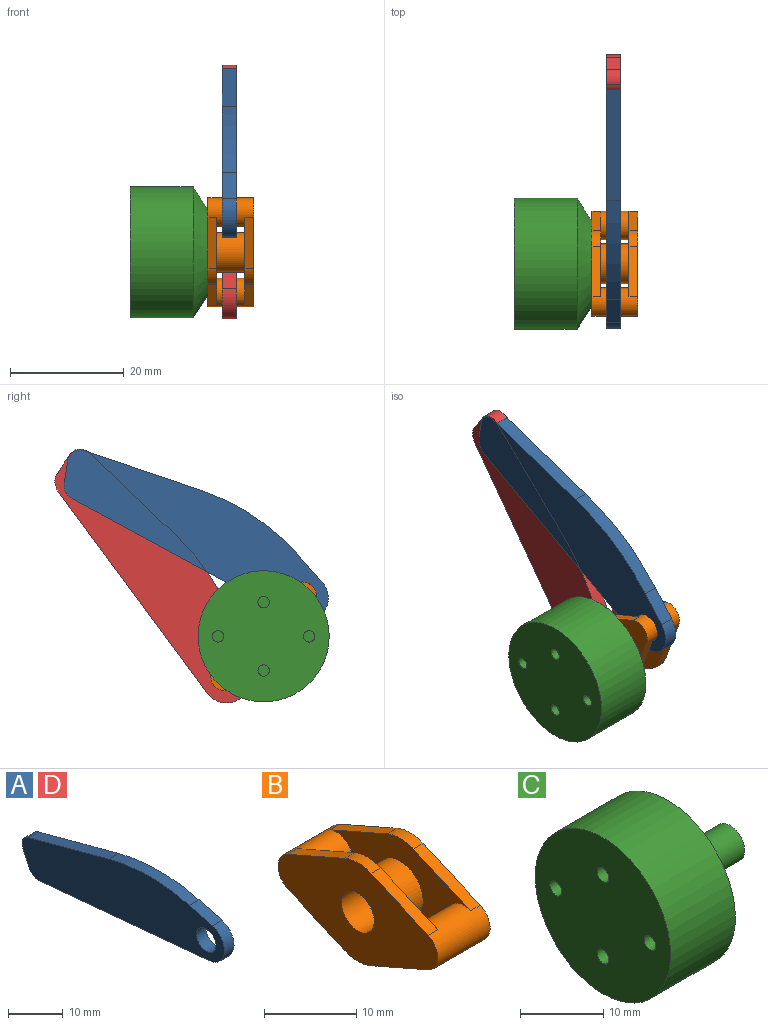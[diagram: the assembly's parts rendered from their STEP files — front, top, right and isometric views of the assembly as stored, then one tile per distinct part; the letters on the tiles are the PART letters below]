
ASSEMBLY  parts=4 mates=3
PART A: 11 faces, bbox 2.5x52.3x15.2 mm
  f0: plane 3.51x2.5mm, normal (0,0.91,-0.42), area 9.7mm2, adj f1,f7,f8,f9
  f1: cylinder r=2.28mm len=3.16mm, axis (-1,0,0), area 9.9mm2, adj f0,f2,f8,f9
  f2: plane 20.79x5.58mm, normal (0,0.26,0.97), area 53.8mm2, adj f1,f3,f8,f9
  f3: cylinder r=40.06mm len=20.78mm, axis (-1,0,0), area 52.5mm2, adj f2,f4,f8,f9
  f4: plane 5.97x2.5mm, normal (0,-0.26,0.97), area 15.5mm2, adj f3,f5,f8,f9
  f5: cylinder r=4.16mm len=8.15mm, axis (-1,0,0), area 29mm2, adj f4,f6,f8,f9
  f6: plane 43.96x4.06mm, normal (0,-0.09,-1), area 110.4mm2, adj f5,f7,f8,f9
  f7: cylinder r=2.72mm len=2.71mm, axis (-1,0,0), area 8.3mm2, adj f0,f6,f8,f9
  f8: plane 52.3x15.2mm, normal (1,0,0), area 524.7mm2, adj f0,f1,f2,f3,f4,f5,f6,f7
  f9: plane 52.3x15.2mm, normal (-1,0,0), area 524.7mm2, adj f0,f1,f2,f3,f4,f5,f6,f7
  f10: cylinder r=2.5mm len=5mm, axis (1,0,0), area 39.3mm2, adj f8,f9
PART B: 20 faces, bbox 8x24.5x13.1 mm
  f0: plane 8.76x3.83mm, normal (0,-0.4,0.92), area 14.3mm2, adj f7,f14,f15,f19
  f1: plane 8.76x3.83mm, normal (0,-0.4,-0.92), area 14.3mm2, adj f2,f7,f16,f18
  f2: cylinder r=5mm len=4.01mm, axis (-1,0,0), area 6.2mm2, adj f1,f10,f16,f18
  f3: plane 8.76x3.83mm, normal (0,0.4,-0.92), area 14.3mm2, adj f9,f11,f15,f19
  f4: plane 8.76x3.83mm, normal (0,0.4,0.92), area 14.3mm2, adj f5,f11,f16,f18
  f5: cylinder r=5mm len=4.01mm, axis (-1,0,0), area 6.2mm2, adj f4,f6,f16,f18
  f6: plane 8.76x3.83mm, normal (0,-0.4,0.92), area 14.3mm2, adj f5,f7,f16,f18
  f7: cylinder r=2.5mm len=8mm, axis (-1,0,0), area 95.9mm2, adj f0,f1,f6,f8,f15,f16,f18,f19
  f8: plane 8.76x3.83mm, normal (0,-0.4,-0.92), area 14.3mm2, adj f7,f9,f15,f19
  f9: cylinder r=5mm len=4.01mm, axis (-1,0,0), area 6.2mm2, adj f3,f8,f15,f19
  f10: plane 8.76x3.83mm, normal (0,0.4,-0.92), area 14.3mm2, adj f2,f11,f16,f18
  f11: cylinder r=2.5mm len=8mm, axis (-1,0,0), area 95.9mm2, adj f3,f4,f10,f12,f15,f16,f18,f19
  f12: plane 8.76x3.83mm, normal (0,0.4,0.92), area 14.3mm2, adj f11,f14,f15,f19
  f13: cylinder r=2.5mm len=8mm, axis (-1,0,0), area 125.7mm2, adj f15,f16
  f14: cylinder r=5mm len=4.01mm, axis (-1,0,0), area 6.2mm2, adj f0,f12,f15,f19
  f15: plane 24.53x13.09mm, normal (1,0,0), area 189mm2, adj f0,f3,f7,f8,f9,f11,f12,f13
  f16: plane 24.53x13.09mm, normal (-1,0,0), area 189mm2, adj f1,f2,f4,f5,f6,f7,f10,f11
  f17: cylinder r=3.5mm len=7mm, axis (1,0,0), area 110mm2, adj f18,f19
  f18: plane 21.53x13.09mm, normal (1,0,0), area 130.9mm2, adj f1,f2,f4,f5,f6,f7,f10,f11
  f19: plane 21.53x13.09mm, normal (-1,0,0), area 130.9mm2, adj f0,f3,f7,f8,f9,f11,f12,f14
PART C: 14 faces, bbox 21.6x23x23 mm
  f0: cylinder r=11.5mm len=23mm, axis (-1,0,0), area 794.8mm2, adj f2,f3
  f1: plane 15x15mm, normal (1,0,0), area 157.1mm2, adj f3,f4
  f2: plane 23x23mm, normal (-1,0,0), area 402.9mm2, adj f0,f6,f8,f10,f12
  f3: cone r=7.5mm half-angle=57deg, axis (-1,0,0), area 284.8mm2, adj f0,f1
  f4: cylinder r=2.5mm len=8mm, axis (-1,0,0), area 125.7mm2, adj f1,f5
  f5: plane 5x5mm, normal (1,0,0), area 19.6mm2, adj f4
  f6: cylinder r=1mm len=3mm, axis (-1,0,0), area 18.8mm2, adj f2,f7
  f7: plane 2x2mm, normal (-1,0,0), area 3.1mm2, adj f6
  f8: cylinder r=1mm len=3mm, axis (-1,0,0), area 18.8mm2, adj f2,f9
  f9: plane 2x2mm, normal (-1,0,0), area 3.1mm2, adj f8
  f10: cylinder r=1mm len=3mm, axis (-1,0,0), area 18.8mm2, adj f2,f11
  f11: plane 2x2mm, normal (-1,0,0), area 3.1mm2, adj f10
  f12: cylinder r=1mm len=3mm, axis (-1,0,0), area 18.8mm2, adj f2,f13
  f13: plane 2x2mm, normal (-1,0,0), area 3.1mm2, adj f12
PART D: same geometry as A
PLACE A rot(axis=(1,0,0),33.8deg) t=(56.15,-16.02,17.86)mm
PLACE B rot(axis=(1,0,0),133.8deg) t=(53.65,-16.87,-4.33)mm
PLACE C t=(40.05,-105.35,-26.66)mm fixed
PLACE D rot(axis=(1,0,0),58.8deg) t=(56.15,-9.62,5.57)mm
MATE revolute C.f0 <-> B.f13  axis (-1,0,0) through (53.65,-16.87,-4.33)mm
MATE revolute A.f10 <-> B.f11  axis (1,0,0) through (58.65,-23.62,2.71)mm
MATE revolute D.f10 <-> B.f7  axis (1,0,0) through (58.65,-10.11,-11.38)mm
